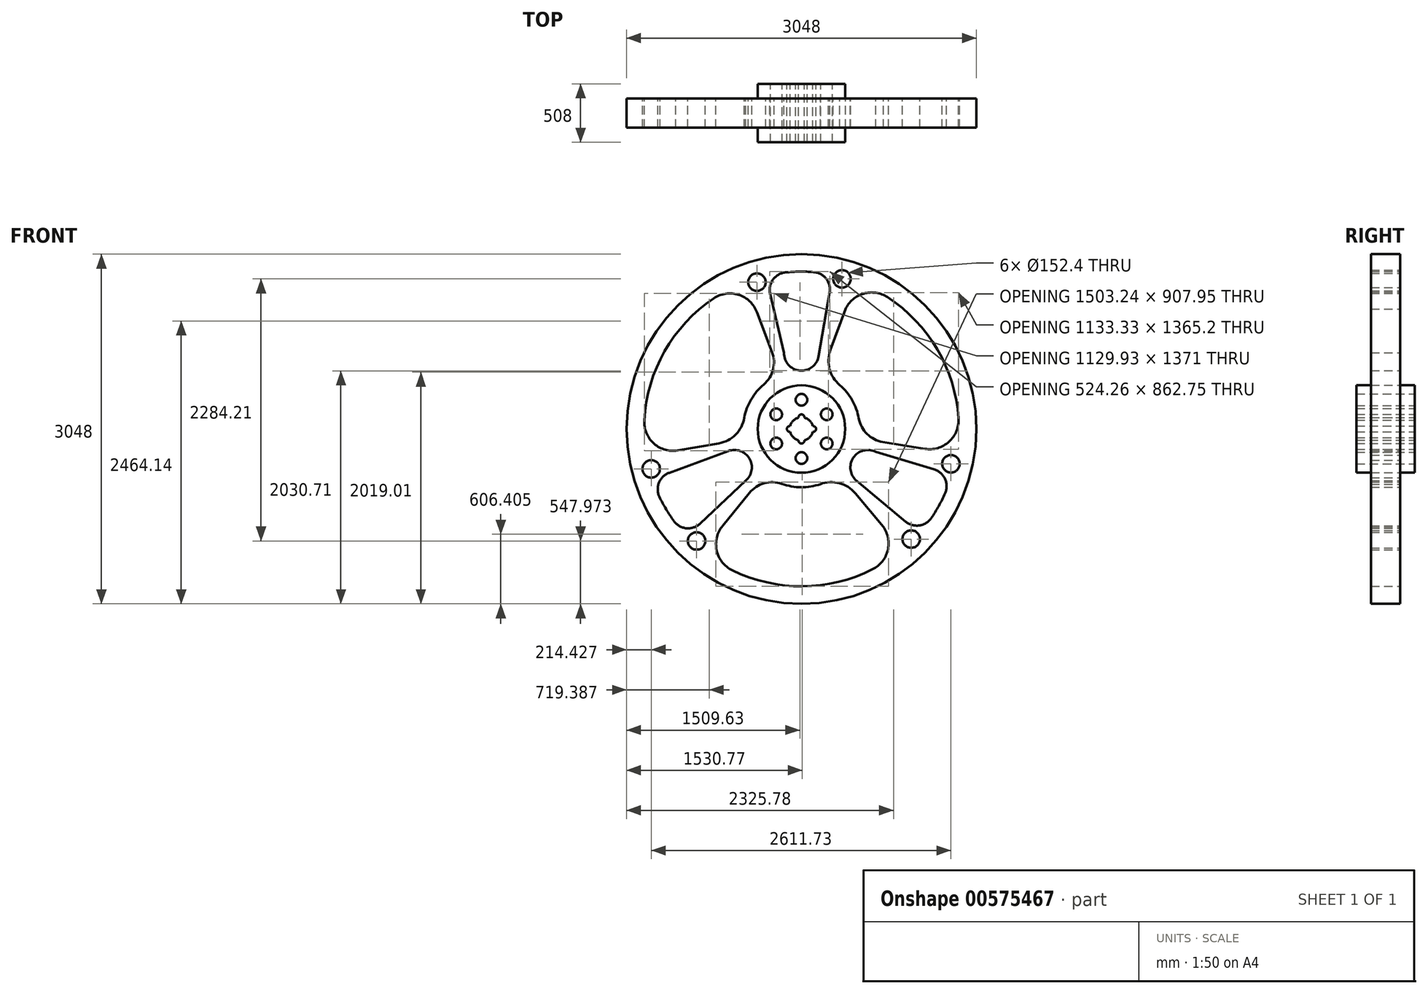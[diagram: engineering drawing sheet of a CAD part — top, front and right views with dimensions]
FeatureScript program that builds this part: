
annotation { "Feature Type Name" : "Feature", "Feature Type Description" : "" }
export const myFeature = defineFeature(function(context is Context, id is Id, definition is map)
    precondition{}
    {
        {
            var Q0;
            Q0=qCreatedBy(makeId("Front.planeOp"),FACE);
            var sketch = newSketch(context, id + "F0", { "sketchPlane" : qUnion([Q0])});
            skCircle(sketch, "E0", {"center": v(0, 0) * mm, "radius": 1524 * mm});
            skArc(sketch, "E1", {"start": v(-603.66, -1231.62) * mm, "mid": v(9.32, -1371.57) * mm, "end": v(620.35, -1223.3) * mm});
            skArc(sketch, "E2", {"start": v(-170.92, -478.38) * mm, "mid": v(-324.7, -472.93) * mm, "end": v(-453.41, -557.27) * mm});
            skArc(sketch, "E3", {"start": v(-686.88, -844.22) * mm, "mid": v(-739.25, -1058.1) * mm, "end": v(-603.66, -1231.62) * mm});
            skArc(sketch, "E4", {"start": v(468.27, -560.7) * mm, "mid": v(329.32, -472.29) * mm, "end": v(164.83, -480.52) * mm});
            skArc(sketch, "E5", {"start": v(620.35, -1223.3) * mm, "mid": v(751.02, -1059.31) * mm, "end": v(712.55, -853.2) * mm});
            skArc(sketch, "E6.trimOffspring", {"start": v(-170.92, -478.38) * mm, "mid": v(-3.23, -507.99) * mm, "end": v(164.83, -480.52) * mm});
            skArc(sketch, "E7.trimOffspring", {"start": v(1130.5, -776.7) * mm, "mid": v(1195.85, -671.73) * mm, "end": v(1251.5, -561.3) * mm});
            skCircle(sketch, "E8", {"center": v(0, 0) * mm, "radius": 381 * mm});
            skLineSegment(sketch, "E9", {"start": v(-453.41, -557.27) * mm, "end": v(-689.7, -847.68) * mm});
            skLineSegment(sketch, "E10", {"start": v(468.27, -560.7) * mm, "end": v(712.55, -853.2) * mm});
            skArc(sketch, "E11.1.0", {"start": v(749.23, 1148.88) * mm, "mid": v(541.89, 1180.06) * mm, "end": v(382.61, 1043.68) * mm});
            skLineSegment(sketch, "E11.1.1", {"start": v(251.44, 685.88) * mm, "end": v(382.61, 1043.68) * mm});
            skArc(sketch, "E11.1.2", {"start": v(251.44, 685.88) * mm, "mid": v(244.35, 521.34) * mm, "end": v(333.72, 383) * mm});
            skArc(sketch, "E11.1.3", {"start": v(499.75, 91.17) * mm, "mid": v(441.55, 251.2) * mm, "end": v(333.72, 383) * mm});
            skArc(sketch, "E11.1.4", {"start": v(499.75, 91.17) * mm, "mid": v(571.92, -44.74) * mm, "end": v(709.31, -114.03) * mm});
            skLineSegment(sketch, "E11.1.5", {"start": v(709.31, -114.03) * mm, "end": v(1078.97, -173.46) * mm});
            skArc(sketch, "E11.1.6", {"start": v(1074.56, -172.75) * mm, "mid": v(1285.97, -111.16) * mm, "end": v(1368.44, 93.02) * mm});
            skArc(sketch, "E11.1.7", {"start": v(1368.44, 93.02) * mm, "mid": v(1183.15, 693.86) * mm, "end": v(749.23, 1148.88) * mm});
            skArc(sketch, "E11.2.0", {"start": v(-1369.58, 74.41) * mm, "mid": v(-1292.9, -120.74) * mm, "end": v(-1095.16, -190.49) * mm});
            skLineSegment(sketch, "E11.2.1", {"start": v(-719.71, -125.18) * mm, "end": v(-1095.16, -190.49) * mm});
            skArc(sketch, "E11.2.2", {"start": v(-719.71, -125.18) * mm, "mid": v(-573.67, -49.05) * mm, "end": v(-498.55, 97.51) * mm});
            skArc(sketch, "E11.2.3", {"start": v(-328.83, 387.22) * mm, "mid": v(-438.32, 256.8) * mm, "end": v(-498.55, 97.51) * mm});
            skArc(sketch, "E11.2.4", {"start": v(-328.83, 387.22) * mm, "mid": v(-247.22, 517.67) * mm, "end": v(-255.9, 671.3) * mm});
            skLineSegment(sketch, "E11.2.5", {"start": v(-255.9, 671.3) * mm, "end": v(-389.26, 1021.14) * mm});
            skArc(sketch, "E11.2.6", {"start": v(-387.67, 1016.97) * mm, "mid": v(-546.72, 1169.27) * mm, "end": v(-764.78, 1138.6) * mm});
            skArc(sketch, "E11.2.7", {"start": v(-764.78, 1138.6) * mm, "mid": v(-1192.47, 677.71) * mm, "end": v(-1369.58, 74.41) * mm});
            skLineSegment(sketch, "E12", {"start": v(149.83, 634.2) * mm, "end": v(250.12, 1215.46) * mm});
            skLineSegment(sketch, "E13", {"start": v(-134.05, 588.3) * mm, "end": v(-272.5, 1178.03) * mm});
            skArc(sketch, "E14", {"start": v(-139.65, 1364.47) * mm, "mid": v(-248.24, 1301.3) * mm, "end": v(-272.5, 1178.03) * mm});
            skArc(sketch, "E15", {"start": v(245.65, 1189.55) * mm, "mid": v(215.79, 1309) * mm, "end": v(107.4, 1367.39) * mm});
            skLineSegment(sketch, "E16.1.0", {"start": v(-637.9, -192.4) * mm, "end": v(-1177.67, -391.12) * mm});
            skArc(sketch, "E16.1.1", {"start": v(-1153, -382.04) * mm, "mid": v(-1241.51, -467.62) * mm, "end": v(-1237.9, -590.69) * mm});
            skArc(sketch, "E16.1.2", {"start": v(-1111.84, -803.17) * mm, "mid": v(-1002.84, -865.64) * mm, "end": v(-883.96, -825) * mm});
            skLineSegment(sketch, "E16.1.3", {"start": v(-476.98, -442.67) * mm, "end": v(-883.96, -825) * mm});
            skLineSegment(sketch, "E16.2.0", {"start": v(481.12, -452.53) * mm, "end": v(927.56, -824.33) * mm});
            skArc(sketch, "E16.2.1", {"start": v(907.35, -807.5) * mm, "mid": v(1025.73, -841.37) * mm, "end": v(1130.5, -776.7) * mm});
            skArc(sketch, "E16.2.2", {"start": v(1251.5, -561.3) * mm, "mid": v(1251.08, -435.67) * mm, "end": v(1156.46, -353.03) * mm});
            skLineSegment(sketch, "E16.2.3", {"start": v(596.4, -184.06) * mm, "end": v(1156.46, -353.03) * mm});
            skArc(sketch, "E17.trimOffspring", {"start": v(107.4, 1367.39) * mm, "mid": v(-16.2, 1371.5) * mm, "end": v(-139.65, 1364.47) * mm});
            skArc(sketch, "E18.trimOffspring", {"start": v(-1237.9, -590.69) * mm, "mid": v(-1179.66, -699.77) * mm, "end": v(-1111.84, -803.17) * mm});
            skArc(sketch, "E19", {"start": v(-151.98, 664.65) * mm, "mid": v(-15.26, 508.77) * mm, "end": v(149.83, 634.2) * mm});
            skPoint(sketch, "E20.orphan", {"position": v(125.35, 492.3) * mm});
            skArc(sketch, "E21", {"start": v(647.57, -199.5) * mm, "mid": v(451.33, -251.67) * mm, "end": v(481.12, -452.53) * mm});
            skArc(sketch, "E22.trimOffspring", {"start": v(430.76, -283.5) * mm, "mid": v(439.72, -270.15) * mm, "end": v(448.26, -256.53) * mm});
            skArc(sketch, "E23", {"start": v(-484.95, -450.17) * mm, "mid": v(-454.18, -257.65) * mm, "end": v(-637.9, -192.4) * mm});
            skPoint(sketch, "E24.orphan", {"position": v(-372.94, -344.94) * mm});
            skPoint(sketch, "E25.orphan", {"position": v(-489.01, -137.59) * mm});
            skCircle(sketch, "E26", {"center": v(353.31, 1308.18) * mm, "radius": 76.2 * mm});
            skCircle(sketch, "E27", {"center": v(-388.37, 1279.38) * mm, "radius": 76.2 * mm});
            skCircle(sketch, "E28.1.0", {"center": v(-1309.57, -348.11) * mm, "radius": 76.2 * mm});
            skCircle(sketch, "E28.1.1", {"center": v(-913.79, -976.03) * mm, "radius": 76.2 * mm});
            skCircle(sketch, "E28.2.0", {"center": v(956.26, -960.07) * mm, "radius": 76.2 * mm});
            skCircle(sketch, "E28.2.1", {"center": v(1302.16, -303.35) * mm, "radius": 76.2 * mm});
            skPoint(sketch, "E29.centerSnap0", {"position": v(-247.22, 517.67) * mm});
            skPoint(sketch, "E30.centerSnap0", {"position": v(-15.26, 508.77) * mm});
            skPoint(sketch, "E31.centerSnap0", {"position": v(-3.23, -507.99) * mm});
            skCircle(sketch, "E32", {"center": v(0, 254) * mm, "radius": 50.8 * mm});
            skCircle(sketch, "E33.1.0", {"center": v(-219.97, -127) * mm, "radius": 50.8 * mm});
            skCircle(sketch, "E33.2.0", {"center": v(219.97, -127) * mm, "radius": 50.8 * mm});
            skCircle(sketch, "E34", {"center": v(0, -254) * mm, "radius": 50.8 * mm});
            skCircle(sketch, "E35.1.0", {"center": v(219.97, 127) * mm, "radius": 50.8 * mm});
            skCircle(sketch, "E35.2.0", {"center": v(-219.97, 127) * mm, "radius": 50.8 * mm});
            skCircle(sketch, "E36", {"center": v(0, 0) * mm, "radius": 101.6 * mm});
            skArc(sketch, "E37", {"start": v(25.2, 98.42) * mm, "mid": v(0, 127) * mm, "end": v(-25.2, 98.43) * mm});
            skArc(sketch, "E38", {"start": v(-25.2, -98.42) * mm, "mid": v(0, -127) * mm, "end": v(25.2, -98.43) * mm});
            skArc(sketch, "E39", {"start": v(98.42, -25.2) * mm, "mid": v(127, 0) * mm, "end": v(98.43, 25.2) * mm});
            skArc(sketch, "E40", {"start": v(-98.43, 25.2) * mm, "mid": v(-127, 0) * mm, "end": v(-98.43, -25.2) * mm});
            skSolve(sketch);
        }
        {
            var Q0;
            Q0=makeQuery(id+"F0.imprint","IMPRINT",FACE,{"disambiguationData":[TD([[makeQuery(id+"F0.imprint","IMPRINT",EDGE,{"derivedFrom":sQuery(id+"F0.wireOp",EDGE,"E0")}),1.0]])]});
            extrude(context, id + "F1", {"entities" : qUnion([Q0]), "depth" : 254 * mm, "offsetDistance" : 25.4 * mm, "symmetric" : true});
        }
        {
            var Q0;
            Q0=makeQuery(id+"F0.imprint","IMPRINT",FACE,{"disambiguationData":[TD([[makeQuery(id+"F0.imprint","IMPRINT",EDGE,{"derivedFrom":sQuery(id+"F0.wireOp",EDGE,"E8")}),1.0]])]});
            extrude(context, id + "F2", {"entities" : qUnion([Q0]), "operationType" : NewBodyOperationType.ADD, "depth" : 508 * mm, "offsetDistance" : 25.4 * mm, "symmetric" : true});
        }
    });
